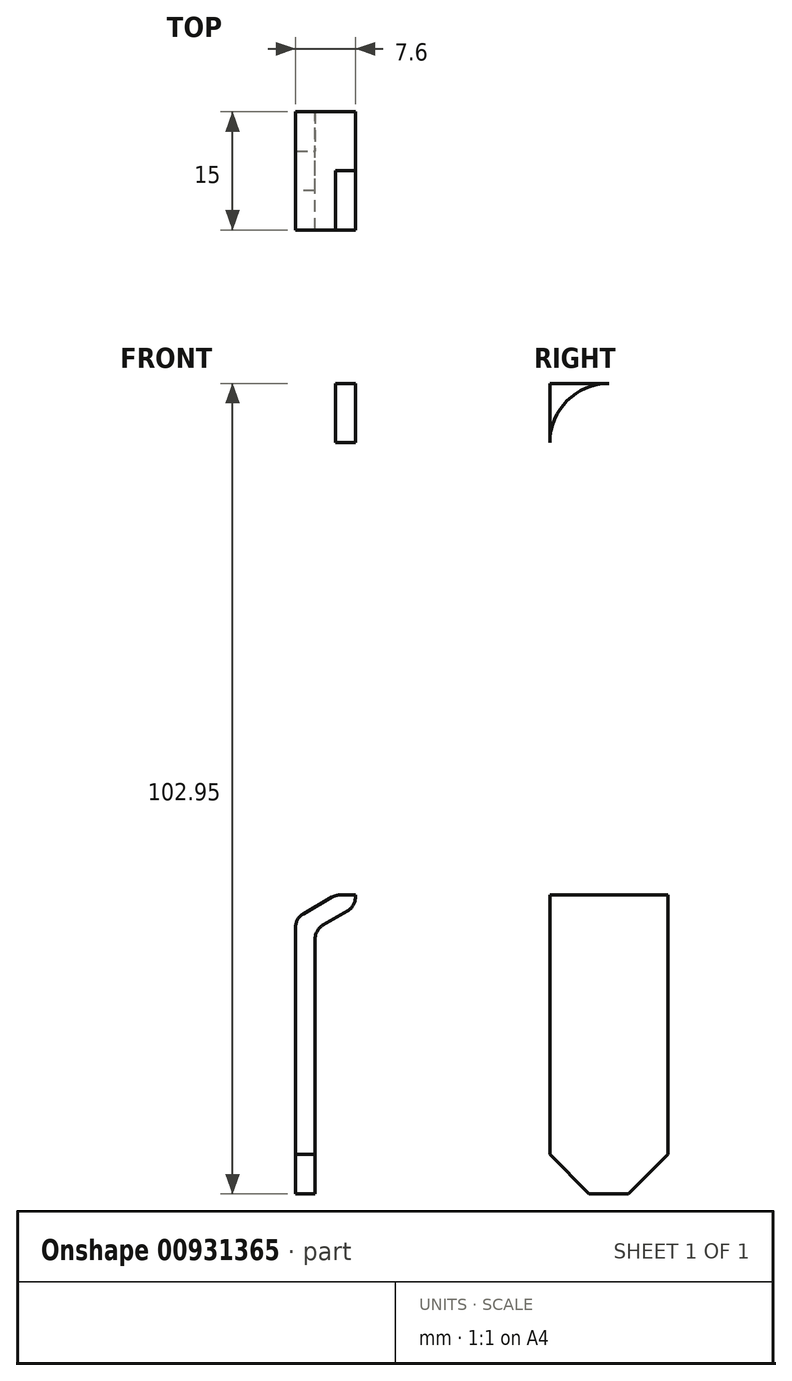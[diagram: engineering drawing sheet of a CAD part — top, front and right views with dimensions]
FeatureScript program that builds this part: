
annotation { "Feature Type Name" : "Feature", "Feature Type Description" : "" }
export const myFeature = defineFeature(function(context is Context, id is Id, definition is map)
    precondition{}
    {
        {
            var Q0;
            Q0=qCreatedBy(makeId("Front.planeOp"),FACE);
            var sketch = newSketch(context, id + "F0", { "sketchPlane" : qUnion([Q0])});
            skLineSegment(sketch, "E0", {"start": v(0, 0) * mm, "end": v(5.1, 2.94) * mm});
            skLineSegment(sketch, "E1", {"start": v(5.1, 2.94) * mm, "end": v(5.1, 69.39) * mm});
            skLineSegment(sketch, "E2", {"start": v(5.1, 69.39) * mm, "end": v(2.6, 69.39) * mm});
            skLineSegment(sketch, "E3", {"start": v(2.6, 69.39) * mm, "end": v(2.6, 4.39) * mm});
            skLineSegment(sketch, "E4", {"start": v(2.6, 4.39) * mm, "end": v(-2.5, 1.44) * mm});
            skLineSegment(sketch, "E5", {"start": v(-2.5, 1.44) * mm, "end": v(-2.5, -33.56) * mm});
            skLineSegment(sketch, "E6", {"start": v(-2.5, -33.56) * mm, "end": v(0, -33.56) * mm});
            skLineSegment(sketch, "E7", {"start": v(0, -33.56) * mm, "end": v(0, 0) * mm});
            skSolve(sketch);
        }
        {
            var Q0;
            Q0 = qSketchRegion(id + "F0", true);
            extrude(context, id + "F1", {"entities" : qUnion([Q0]), "endBound" : BoundingType.SYMMETRIC, "depth" : 15 * mm, "offsetDistance" : 25 * mm});
        }
        {
            var Q0;
            Q0=makeQuery(id+"F1.opExtrude","SWEPT_FACE",FACE,{"disambiguationData":[OSD([sQuery(id+"F0.wireOp",EDGE,"E3")])]});
            var sketch = newSketch(context, id + "F2", { "sketchPlane" : qUnion([Q0])});
            skLineSegment(sketch, "E8", {"start": v(0, 69.39) * mm, "end": v(0, 43.07) * mm, "construction": true});
            skArc(sketch, "E9", {"start": v(-7.5, 61.89) * mm, "mid": v(-5.3, 67.2) * mm, "end": v(0, 69.39) * mm});
            skArc(sketch, "E10", {"start": v(0, 69.39) * mm, "mid": v(5.3, 67.2) * mm, "end": v(7.5, 61.89) * mm});
            skLineSegment(sketch, "E11", {"start": v(-7.5, 61.89) * mm, "end": v(-7.5, 69.39) * mm});
            skLineSegment(sketch, "E12", {"start": v(-7.5, 69.39) * mm, "end": v(0, 69.39) * mm});
            skLineSegment(sketch, "E13", {"start": v(7.5, 69.39) * mm, "end": v(7.5, 61.89) * mm});
            skCircle(sketch, "E14", {"center": v(0, 62.39) * mm, "radius": 5 * mm});
            skSolve(sketch);
        }
        {
            var Q0;
            Q0 = qSketchRegion(id + "F2", true);
            var Q1;
            {var subQ0=sQuery(id+"F2.wireOp",EDGE,"E10");Q1=makeQuery(id+"F2.imprint","IMPRINT",FACE,{"disambiguationData":[TD([[makeQuery(id+"F2.imprint","IMPRINT",EDGE,{"derivedFrom":subQ0}),1.0]])]});}
            extrude(context, id + "F3", {"entities" : qUnion([Q0, Q1]), "operationType" : NewBodyOperationType.REMOVE, "oppositeDirection" : true, "depth" : 25 * mm, "offsetDistance" : 25 * mm});
        }
        {
            var Q0;
            Q0=makeQuery(id+"F1.opExtrude","CAP_EDGE",EDGE,{"disambiguationData":[OSD([sQuery(id+"F0.wireOp",EDGE,"E6")])],"isStart":true});
            var Q1;
            Q1=makeQuery(id+"F1.opExtrude","CAP_EDGE",EDGE,{"disambiguationData":[OSD([sQuery(id+"F0.wireOp",EDGE,"E6")])],"isStart":false});
            chamfer(context, id + "F4", {"entities" : qUnion([Q0, Q1]), "width" : 5 * mm, "tangentPropagation" : true});
        }
        {
            var Q0;
            Q0=makeQuery(id+"F1.opExtrude","SWEPT_EDGE",EDGE,{"disambiguationData":[OSD([sQuery(id+"F0.wireOp",EDGE,"E4"),sQuery(id+"F0.wireOp",EDGE,"E5")])]});
            var Q1;
            Q1=makeQuery(id+"F1.opExtrude","SWEPT_EDGE",EDGE,{"disambiguationData":[OSD([sQuery(id+"F0.wireOp",EDGE,"E3"),sQuery(id+"F0.wireOp",EDGE,"E4")])]});
            var Q2;
            Q2=makeQuery(id+"F1.opExtrude","SWEPT_EDGE",EDGE,{"disambiguationData":[OSD([sQuery(id+"F0.wireOp",EDGE,"E0"),sQuery(id+"F0.wireOp",EDGE,"E1")])]});
            var Q3;
            Q3=makeQuery(id+"F1.opExtrude","SWEPT_EDGE",EDGE,{"disambiguationData":[OSD([sQuery(id+"F0.wireOp",EDGE,"E0"),sQuery(id+"F0.wireOp",EDGE,"E7")])]});
            fillet(context, id + "F5", {"entities" : qUnion([Q0, Q1, Q2, Q3]), "radius" : 2 * mm, "tangentPropagation" : true, "allowEdgeOverflow" : false});
        }
    });
